# Revit family: Franke_Unterthekenkühleinheit_UT12_EC-A600_MS_EC_A600_FM_EC_A800_FM_EC
name_source: partatom
category: Sonderausstattung
revit_build: Autodesk Revit 2015 (Build: 20140606_1530(x64)
units: mm (PartAtom-declared; Revit-internal decimal feet)

## types (1)
- Unterthekenkühleinheit UT12 EC-A600 MS EC,A600 FM EC,A800 FM EC(230V/EU)
    Anzahl der Nullleiter = 1
    Anzahl der Schutzleiter = 1
    Anzahl von Polen = 1
    Aufstellgewicht = 26 kg
    Bauelement = Beistellgerät Unterthekenkühleinheit UT12
    Baugruppenkennzeichen = Beistellgerät Unterthekenkühleinheit UT12
    Beschreibung = Beistellgerät Unterthekenkühleinheit UT12 dient zum Aufbewahren von gekühlter Milch
    Breite = 340 mm  [stored 1.11549 ft]
    Energieverlust nach DIN18873 = 0.783 kWh/24 h - 230 V
    Hersteller = Franke
    Höhe = 544 mm  [stored 1.78478 ft]
    Kosten = 0 $
    Milchvorrat = 12 l
    Modell = 410880 - Unterthekenkühleinheit UT12 EC - A600 MS EC, A600 FM EC, A800 FM EC
    Netzfrequenz = 50 Hz
    Netzfrequenz alternativ = 60 Hz
    Sicherung = 10 A
    Spannung = 230 V
    Stromaufnahme = 0.72 A
    Temperaturbereich = + 3° bis + 8°
    Tiefe = 475 mm  [stored 1.5584 ft]
    URL = http://www.franke.com

note: [stored X ft] marks values corroborated as IEEE doubles in the binary element streams (Revit-internal decimal feet)
